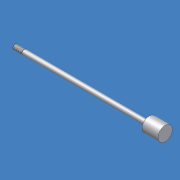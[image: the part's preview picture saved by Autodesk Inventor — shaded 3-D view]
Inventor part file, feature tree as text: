
AUTODESK INVENTOR PART (.ipt)
format: ipt  version: 2012 (Build 160160000, 160)  size: 124,928 bytes
history: native  units: mm (DEFAULTED — no unit token found)
features: other x84, revolve x3, sketch x3, thread x1
ambient origin geometry x8: Origin, YZ Plane, XZ Plane, XY Plane, X Axis, Y Axis, Z Axis, Center Point
bodies: Solid1 (feature_tree)
feature tree (91):
  revolve  "Revolution1"  Angle=360.0deg
  revolve  "Revolution2"  Angle=360.0deg
  thread  "Thread1"  [1 undecoded]
  revolve  "Revolution3"  [1 undecoded]
  other  "rod_cp_XY"
  other  "rod_cp_YZ"
  other  "rod_cp_ZX"
  other  "rod_cp_X"
  other  "rod_cp_Y"
  other  "rod_cp_Z"
  other  "rod_cp_Center"
  other  "to_rod_clevis_XY"
  other  "to_rod_clevis_YZ"
  other  "to_rod_clevis_ZX"
  other  "to_rod_clevis_X"
  other  "to_rod_clevis_Y"
  other  "to_rod_clevis_Z"
  other  "to_rod_clevis_Center"
  other  "rl2_XY"
  other  "rl2_YZ"
  other  "rl2_ZX"
  other  "rl2_X"
  other  "rl2_Y"
  other  "rl2_Z"
  other  "rl2_Center"
  other  "rl1_XY"
  other  "rl1_YZ"
  other  "rl1_ZX"
  other  "rl1_X"
  other  "rl1_Y"
  other  "rl1_Z"
  other  "rl1_Center"
  other  "thd1_XY"
  other  "thd1_YZ"
  other  "thd1_ZX"
  other  "thd1_X"
  other  "thd1_Y"
  other  "thd1_Z"
  other  "thd1_Center"
  other  "thd2_XY"
  other  "thd2_YZ"
  other  "thd2_ZX"
  other  "thd2_X"
  other  "thd2_Y"
  other  "thd2_Z"
  other  "thd2_Center"
  other  "dia1_XY"
  other  "dia1_YZ"
  other  "dia1_ZX"
  other  "dia1_X"
  other  "dia1_Y"
  other  "dia1_Z"
  other  "dia1_Center"
  other  "dia2_XY"
  other  "dia2_YZ"
  other  "dia2_ZX"
  other  "dia2_X"
  other  "dia2_Y"
  other  "dia2_Z"
  other  "dia2_Center"
  other  "hh1_XY"
  other  "hh1_YZ"
  other  "hh1_ZX"
  other  "hh1_X"
  other  "hh1_Y"
  other  "hh1_Z"
  other  "hh1_Center"
  other  "hh2_XY"
  other  "hh2_YZ"
  other  "hh2_ZX"
  other  "hh2_X"
  other  "hh2_Y"
  other  "hh2_Z"
  other  "hh2_Center"
  other  "dia12_XY"
  other  "dia12_YZ"
  other  "dia12_ZX"
  other  "dia12_X"
  other  "dia12_Y"
  other  "dia12_Z"
  other  "dia12_Center"
  other  "dia22_XY"
  other  "dia22_YZ"
  other  "dia22_ZX"
  other  "dia22_X"
  other  "dia22_Y"
  other  "dia22_Z"
  other  "dia22_Center"
  sketch  "Sketch_1"  dims[d0=360.0deg d1=360.0deg]
  sketch  "Sketch_3"  dims[d2=12.7mm d3=167.4876mm d4=360.0deg]
  sketch  "Sketch_30"
note: 2 required parameter values undecoded (feature->parameter linkage not recoverable at this tier; creation-order binding heuristic only, values carry confidence <= 0.55)
